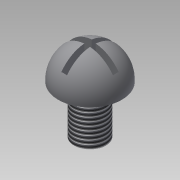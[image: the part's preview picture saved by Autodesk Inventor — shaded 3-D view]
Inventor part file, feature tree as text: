
AUTODESK INVENTOR PART (.ipt)
format: ipt  version: 2016 (Build 200138000, 138)  size: 211,456 bytes
history: native  units: mm
features: sketch x6, extrude x4, revolve x2, projected_geometry x2, thread x1
ambient origin geometry x8: Origin, YZ Plane, XZ Plane, XY Plane, X Axis, Y Axis, Z Axis, Center Point
bodies: Solid1 (feature_tree)
feature tree (15):
  extrude  "Extrusion1"  Depth=3.0mm TaperAngle=0.0deg
  extrude  "Extrusion2"  Depth=0.1mm TaperAngle=0.0deg
  revolve  "Revolution1"  Angle=90.0deg
  extrude  "Extrusion3"  Depth=10.0mm TaperAngle=360.0deg
  revolve  "Revolution2"  [1 undecoded]
  extrude  "Extrusion4"  [1 undecoded]
  thread  "Thread1"  [1 undecoded]
  sketch  "Sketch1"  dims[d0=2.0mm d1=3.0mm d2=0.0mm]
  sketch  "Sketch2"  dims[d3=4.0mm d4=0.1mm d5=0.0mm]
  sketch  "Sketch3"  dims[d6=40.0mm d8=360.0deg d10=90.0deg]
  sketch  "Sketch4"  dims[d11=10.0mm d12=0.0mm d14=40.0mm d15=360.0deg]
  projected_geometry  "Projected Loop2"
  sketch  "Sketch5"  dims[d16=90.0deg d17=10.0mm d18=0.0mm]
  sketch  "Sketch6"  dims[d19=10.0mm d20=0.0mm]
  projected_geometry  "Projected Loop4"
note: 3 required parameter values undecoded (feature->parameter linkage not recoverable at this tier; creation-order binding heuristic only, values carry confidence <= 0.55)